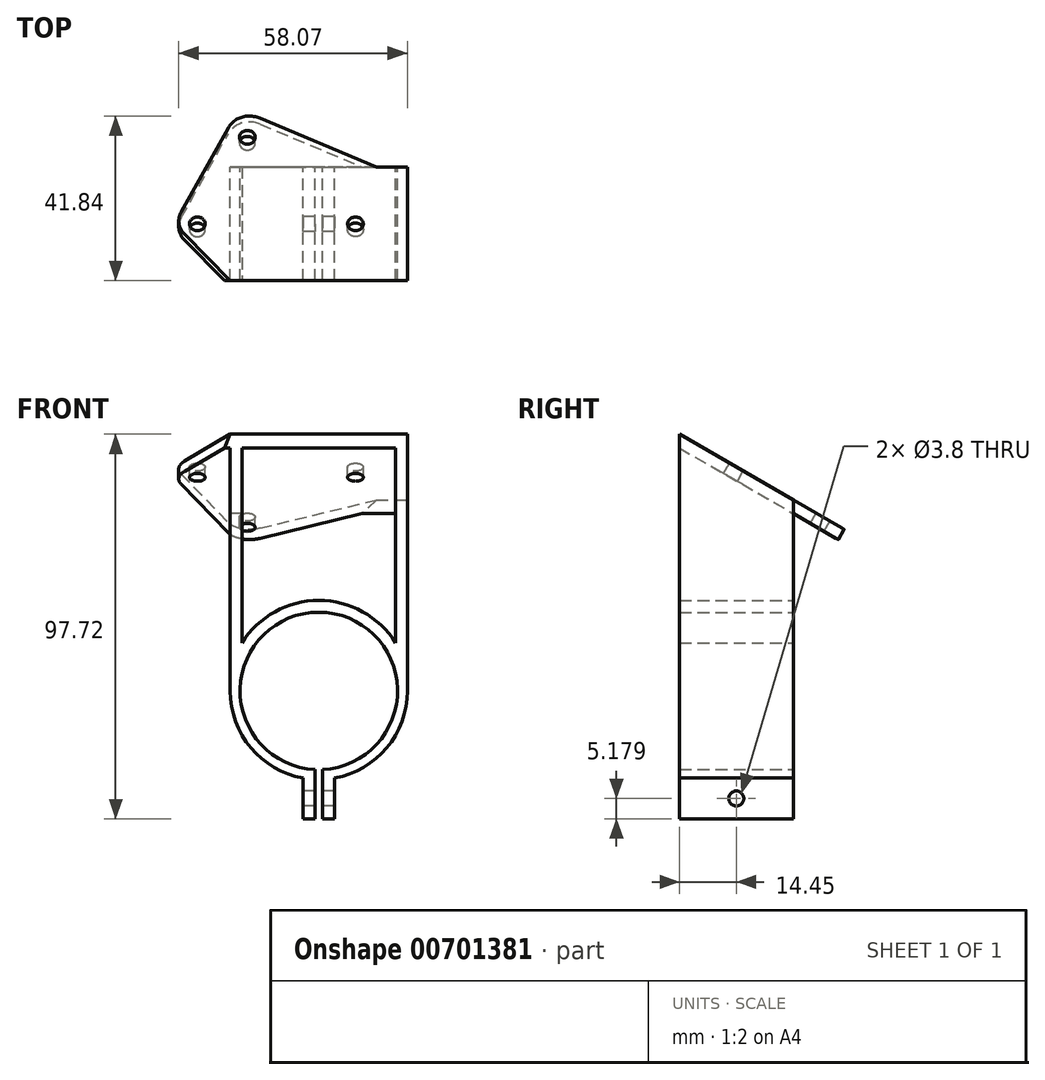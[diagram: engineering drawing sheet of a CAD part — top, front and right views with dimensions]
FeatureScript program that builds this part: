
annotation { "Feature Type Name" : "Feature", "Feature Type Description" : "" }
export const myFeature = defineFeature(function(context is Context, id is Id, definition is map)
    precondition{}
    {
        {
            var Q0;
            Q0=qCreatedBy(makeId("Front.planeOp"),FACE);
            var sketch = newSketch(context, id + "F0", { "sketchPlane" : qUnion([Q0])});
            skCircle(sketch, "E0", {"center": v(0, 0) * mm, "radius": 22.5 * mm});
            skLineSegment(sketch, "E1", {"start": v(-22.5, 0) * mm, "end": v(-22.5, 65.22) * mm});
            skLineSegment(sketch, "E2", {"start": v(22.5, 0) * mm, "end": v(22.5, 65.22) * mm});
            skLineSegment(sketch, "E3", {"start": v(22.5, 65.22) * mm, "end": v(-22.5, 65.22) * mm});
            skPoint(sketch, "E4", {"position": v(0, -22.5) * mm});
            skSolve(sketch);
        }
        {
            var Q0;
            Q0=makeQuery(id+"F0.imprint","IMPRINT",FACE,{"disambiguationData":[TD([[makeQuery(id+"F0.imprint","IMPRINT",EDGE,{"derivedFrom":sQuery(id+"F0.wireOp",EDGE,"E0")}),1.0]])]});
            var Q1;
            {var subQ0=sQuery(id+"F0.wireOp",EDGE,"E1");Q1=makeQuery(id+"F0.imprint","IMPRINT",FACE,{"disambiguationData":[TD([[makeQuery(id+"F0.imprint","IMPRINT",EDGE,{"derivedFrom":subQ0}),-1.0]])]});}
            extrude(context, id + "F1", {"entities" : qUnion([Q0, Q1]), "depth" : 28.9 * mm, "offsetDistance" : 25 * mm});
        }
        {
            var Q0;
            Q0=sQuery(id+"F0.wireOp",VERTEX,"E0.center");
            var Q1;
            Q1=makeQuery(id+"F1.opExtrude","SWEPT_BODY",BODY,{"disambiguationData":[OSD([sQuery(id+"F0.wireOp",EDGE,"E0")])]});
            hole(context, id + "F2", {"style" : HoleStyle.SIMPLE, "endStyle" : HoleEndStyle.THROUGH, "oppositeDirection" : true, "holeDiameter" : 40 * mm, "majorDiameter" : 5 * mm, "isTappedThrough" : true, "tappedDepth" : 12 * mm, "tapClearance" : 3, "locations" : qUnion([Q0]), "scope" : qUnion([Q1])});
        }
        {
            var Q0;
            Q0=makeQuery(id+"F1.opExtrude","SWEPT_FACE",FACE,{"disambiguationData":[OSD([sQuery(id+"F0.wireOp",EDGE,"E2")])]});
            var sketch = newSketch(context, id + "F3", { "sketchPlane" : qUnion([Q0])});
            skLineSegment(sketch, "E5", {"start": v(-28.9, 65.22) * mm, "end": v(0, 48.53) * mm});
            skSolve(sketch);
        }
        {
            var Q0;
            {var subQ0=sQuery(id+"F3.wireOp",EDGE,"E5");Q0=makeQuery(id+"F3.imprint","IMPRINT",FACE,{"disambiguationData":[TD([[makeQuery(id+"F3.imprint","IMPRINT",EDGE,{"derivedFrom":subQ0}),1.0]])]});}
            extrude(context, id + "F4", {"entities" : qUnion([Q0]), "operationType" : NewBodyOperationType.REMOVE, "endBound" : BoundingType.THROUGH_ALL, "oppositeDirection" : true, "depth" : 25 * mm, "offsetDistance" : 25 * mm});
        }
        {
            var Q0;
            {var subQ0=sQuery(id+"F0.wireOp",EDGE,"E0");var subQ1=makeQuery(id+"F0.imprint","INTERSECT",VERTEX,{"derivedFrom":[subQ0,sQuery(id+"F0.wireOp",EDGE,"E1")]});Q0=makeQuery(id+"F0.imprint","IMPRINT",FACE,{"disambiguationData":[TD([[makeQuery(id+"F0.imprint","IMPRINT",EDGE,{"disambiguationData":[TD([[subQ1,1.0]])],"derivedFrom":subQ0}),1.0]])]});}
            var sketch = newSketch(context, id + "F5", { "sketchPlane" : qUnion([Q0])});
            skLineSegment(sketch, "E6", {"start": v(0, -24.67) * mm, "end": v(0, 0) * mm, "construction": true});
            skLineSegment(sketch, "E7", {"start": v(1, 7.5) * mm, "end": v(1, 0.8) * mm});
            skLineSegment(sketch, "E8.MirrorCS", {"start": v(-1, 7.5) * mm, "end": v(-1, 0.8) * mm});
            skLineSegment(sketch, "E9.bottom", {"start": v(1, 0.8) * mm, "end": v(-1, 0.8) * mm});
            skLineSegment(sketch, "E9.top", {"start": v(1, -32.5) * mm, "end": v(-1, -32.5) * mm});
            skLineSegment(sketch, "E9.left", {"start": v(1, 0.8) * mm, "end": v(1, -32.5) * mm});
            skLineSegment(sketch, "E9.right", {"start": v(-1, 0.8) * mm, "end": v(-1, -32.5) * mm});
            skLineSegment(sketch, "E10.bottom", {"start": v(-1, 7.5) * mm, "end": v(-4, 7.5) * mm});
            skLineSegment(sketch, "E10.top", {"start": v(-1, -32.5) * mm, "end": v(-4, -32.5) * mm});
            skLineSegment(sketch, "E10.left", {"start": v(-1, 7.5) * mm, "end": v(-1, -32.5) * mm});
            skLineSegment(sketch, "E10.right", {"start": v(-4, 7.5) * mm, "end": v(-4, -32.5) * mm});
            skLineSegment(sketch, "E11.MirrorCS", {"start": v(4, 7.5) * mm, "end": v(4, -32.5) * mm});
            skLineSegment(sketch, "E12.MirrorCS", {"start": v(1, 7.5) * mm, "end": v(4, 7.5) * mm});
            skLineSegment(sketch, "E13.MirrorCS", {"start": v(1, -32.5) * mm, "end": v(4, -32.5) * mm});
            skSolve(sketch);
        }
        {
            var Q0;
            {var subQ0=sQuery(id+"F5.wireOp",EDGE,"E13.MirrorCS");Q0=makeQuery(id+"F5.imprint","IMPRINT",FACE,{"disambiguationData":[TD([[makeQuery(id+"F5.imprint","IMPRINT",EDGE,{"derivedFrom":subQ0}),1.0]])]});}
            var Q1;
            {var subQ0=sQuery(id+"F5.wireOp",EDGE,"E10.top");Q1=makeQuery(id+"F5.imprint","IMPRINT",FACE,{"disambiguationData":[TD([[makeQuery(id+"F5.imprint","IMPRINT",EDGE,{"derivedFrom":subQ0}),-1.0]])]});}
            extrude(context, id + "F6", {"entities" : qUnion([Q0, Q1]), "operationType" : NewBodyOperationType.ADD, "depth" : 28.9 * mm, "offsetDistance" : 25 * mm});
        }
        {
            var Q0;
            {var subQ0=sQuery(id+"F5.wireOp",EDGE,"E9.bottom");Q0=makeQuery(id+"F5.imprint","IMPRINT",FACE,{"disambiguationData":[TD([[makeQuery(id+"F5.imprint","IMPRINT",EDGE,{"derivedFrom":subQ0}),1.0]])]});}
            extrude(context, id + "F7", {"entities" : qUnion([Q0]), "operationType" : NewBodyOperationType.REMOVE, "endBound" : BoundingType.THROUGH_ALL, "depth" : 25 * mm, "offsetDistance" : 25 * mm});
        }
        {
            var Q0;
            Q0=makeQuery(id+"F6.opExtrude","SWEPT_FACE",FACE,{"disambiguationData":[OSD([sQuery(id+"F5.wireOp",EDGE,"E10.right")])]});
            var sketch = newSketch(context, id + "F8", { "sketchPlane" : qUnion([Q0])});
            skLineSegment(sketch, "E14", {"start": v(14.45, -22.14) * mm, "end": v(14.45, -32.5) * mm, "construction": true});
            skCircle(sketch, "E15", {"center": v(14.45, -27.32) * mm, "radius": 1.9 * mm});
            skSolve(sketch);
        }
        {
            var Q0;
            Q0=makeQuery(id+"F8.imprint","IMPRINT",FACE,{"disambiguationData":[TD([[makeQuery(id+"F8.imprint","IMPRINT",EDGE,{"derivedFrom":sQuery(id+"F8.wireOp",EDGE,"E15")}),1.0]])]});
            extrude(context, id + "F9", {"entities" : qUnion([Q0]), "operationType" : NewBodyOperationType.REMOVE, "endBound" : BoundingType.THROUGH_ALL, "oppositeDirection" : true, "depth" : 25 * mm, "offsetDistance" : 25 * mm});
        }
        {
            var Q0;
            {var subQ0=sQuery(id+"F0.wireOp",EDGE,"E0");Q0=makeQuery(id+"F6.boolean.opBoolean","MERGE",FACE,{"derivedFrom":[makeQuery(id+"F1.opExtrude","CAP_FACE",FACE,{"disambiguationData":[OSD([subQ0,sQuery(id+"F0.wireOp",EDGE,"E1"),sQuery(id+"F0.wireOp",EDGE,"E2"),sQuery(id+"F0.wireOp",EDGE,"E3")])],"isStart":false}),makeQuery(id+"F6.opExtrude","CAP_FACE",FACE,{"disambiguationData":[OSD([subQ0,sQuery(id+"F5.wireOp",EDGE,"E9.left"),sQuery(id+"F5.wireOp",EDGE,"E11.MirrorCS"),sQuery(id+"F5.wireOp",EDGE,"E13.MirrorCS")])],"isStart":false}),makeQuery(id+"F6.opExtrude","CAP_FACE",FACE,{"disambiguationData":[OSD([subQ0,sQuery(id+"F5.wireOp",EDGE,"E10.top"),sQuery(id+"F5.wireOp",EDGE,"E10.left"),sQuery(id+"F5.wireOp",EDGE,"E10.right")])],"isStart":false})]});}
            var Q1;
            {var subQ0=sQuery(id+"F0.wireOp",EDGE,"E0");Q1=makeQuery(id+"F6.boolean.opBoolean","MERGE",FACE,{"derivedFrom":[makeQuery(id+"F1.opExtrude","CAP_FACE",FACE,{"disambiguationData":[OSD([subQ0,sQuery(id+"F0.wireOp",EDGE,"E1"),sQuery(id+"F0.wireOp",EDGE,"E2"),sQuery(id+"F0.wireOp",EDGE,"E3")])],"isStart":true}),makeQuery(id+"F6.opExtrude","CAP_FACE",FACE,{"disambiguationData":[OSD([subQ0,sQuery(id+"F5.wireOp",EDGE,"E9.left"),sQuery(id+"F5.wireOp",EDGE,"E11.MirrorCS"),sQuery(id+"F5.wireOp",EDGE,"E13.MirrorCS")])],"isStart":true}),makeQuery(id+"F6.opExtrude","CAP_FACE",FACE,{"disambiguationData":[OSD([subQ0,sQuery(id+"F5.wireOp",EDGE,"E10.top"),sQuery(id+"F5.wireOp",EDGE,"E10.left"),sQuery(id+"F5.wireOp",EDGE,"E10.right")])],"isStart":true})]});}
            shell(context, id + "F10", {"entities" : qUnion([Q0, Q1]), "thickness" : 3 * mm});
        }
        {
            var Q0;
            Q0=makeQuery(id+"F4.boolean.opBoolean","COPY",FACE,{"derivedFrom":makeQuery(id+"F4.opExtrude","SWEPT_FACE",FACE,{"disambiguationData":[OSD([sQuery(id+"F3.wireOp",EDGE,"E5")])]})});
            var sketch = newSketch(context, id + "F11", { "sketchPlane" : qUnion([Q0])});
            skCircle(sketch, "E16", {"center": v(-30.85, -40.95) * mm, "radius": 2 * mm});
            skCircle(sketch, "E17", {"center": v(-18.15, -15.55) * mm, "radius": 2 * mm});
            skCircle(sketch, "E18", {"center": v(9.31, -40.95) * mm, "radius": 2 * mm});
            skPoint(sketch, "E19", {"position": v(22.5, -40.95) * mm});
            skLineSegment(sketch, "E20", {"start": v(-22.5, -57.64) * mm, "end": v(-34.14, -43.93) * mm});
            skLineSegment(sketch, "E21", {"start": v(-34.97, -37.43) * mm, "end": v(-22.98, -12.7) * mm});
            skLineSegment(sketch, "E22", {"start": v(-14.97, -9.93) * mm, "end": v(14.6, -24.27) * mm});
            skPoint(sketch, "E23.visualSharp", {"position": v(-36.68, -40.95) * mm});
            skArc(sketch, "E23.filletArc", {"start": v(-34.97, -37.43) * mm, "mid": v(-35.52, -40.8) * mm, "end": v(-34.14, -43.93) * mm});
            skPoint(sketch, "E24.visualSharp", {"position": v(-20.36, -7.3) * mm});
            skArc(sketch, "E24.filletArc", {"start": v(-14.97, -9.93) * mm, "mid": v(-19.55, -9.66) * mm, "end": v(-22.98, -12.7) * mm});
            skSolve(sketch);
        }
        {
            var Q0;
            Q0=makeQuery(id+"F11.imprint","IMPRINT",FACE,{"disambiguationData":[TD([[makeQuery(id+"F11.imprint","IMPRINT",EDGE,{"derivedFrom":sQuery(id+"F11.wireOp",EDGE,"E16")}),-1.0]])]});
            extrude(context, id + "F12", {"entities" : qUnion([Q0]), "operationType" : NewBodyOperationType.ADD, "oppositeDirection" : true, "depth" : 3 * mm, "offsetDistance" : 25 * mm});
        }
        {
            var Q0;
            Q0=makeQuery(id+"F12.opExtrude","SWEPT_FACE",FACE,{"disambiguationData":[OSD([sQuery(id+"F0.wireOp",EDGE,"E1"),sQuery(id+"F3.wireOp",EDGE,"E5")])]});
            var Q1;
            Q1=makeQuery(id+"F1.opExtrude","SWEPT_FACE",FACE,{"disambiguationData":[OSD([sQuery(id+"F0.wireOp",EDGE,"E2")])]});
            extrude(context, id + "F13", {"entities" : qUnion([Q0]), "operationType" : NewBodyOperationType.REMOVE, "oppositeDirection" : true, "depth" : 25 * mm, "endBoundEntityFace" : qUnion([Q1]), "offsetDistance" : 25 * mm});
        }
        {
            var Q0;
            Q0=makeQuery(id+"F11.imprint","IMPRINT",FACE,{"disambiguationData":[TD([[makeQuery(id+"F11.imprint","IMPRINT",EDGE,{"derivedFrom":sQuery(id+"F11.wireOp",EDGE,"E18")}),1.0]])]});
            extrude(context, id + "F14", {"entities" : qUnion([Q0]), "operationType" : NewBodyOperationType.REMOVE, "oppositeDirection" : true, "depth" : 5 * mm, "offsetDistance" : 25 * mm});
        }
    });
